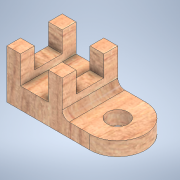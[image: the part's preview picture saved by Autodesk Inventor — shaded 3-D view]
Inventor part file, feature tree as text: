
AUTODESK INVENTOR PART (.ipt)
format: ipt  version: 2020 (Build 240168000, 168)  size: 171,520 bytes
history: native  units: mm
features: sketch x4, extrude x3, hole x1
ambient origin geometry x8: Origin, YZ Plane, XZ Plane, XY Plane, X Axis, Y Axis, Z Axis, Center Point
bodies: Solid1 (feature_tree)
feature tree (8):
  extrude  "Extrusion1"  Depth=44.45mm
  extrude  "Extrusion2"  Depth=19.05mm
  hole  "Hole1"  [1 undecoded]
  extrude  "Extrusion3"  Depth=25.4mm TaperAngle=0.0deg
  sketch  "Sketch1"  dims[d0=76.2mm d1=44.45mm]
  sketch  "Sketch2"  dims[d2=12.7mm d3=19.05mm]
  sketch  "Sketch5"  dims[d4=50.8mm d5=12.7mm]
  sketch  "Sketch6"  dims[d6=50.8mm d7=0.0mm d8=63.5mm d9=0.0mm d11=19.05mm d12=19.05mm d13=9.525mm d14=6.35mm d15=14.3117mm d16=25.4mm d17=20.594885mm d18=6.35mm d19=19.05mm d20=25.4mm d21=63.5mm d22=0.0mm]
note: 1 required parameter value undecoded (feature->parameter linkage not recoverable at this tier; creation-order binding heuristic only, values carry confidence <= 0.55)
